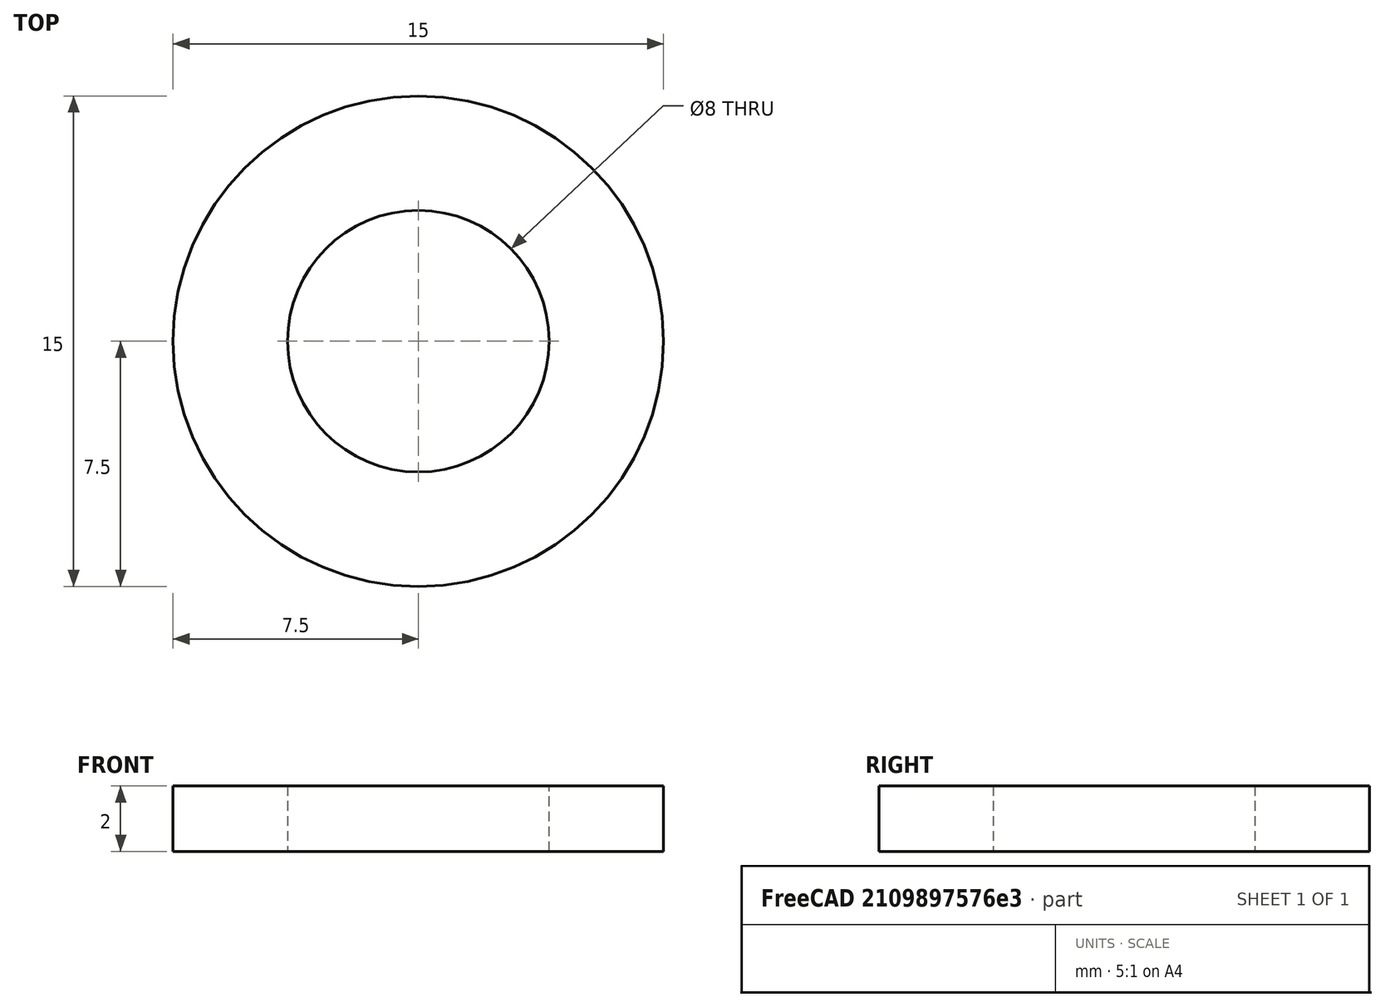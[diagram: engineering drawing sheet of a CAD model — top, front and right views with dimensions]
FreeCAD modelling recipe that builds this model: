
FCSTD DOCUMENT  (FreeCAD 0.19R24276 (Git))
Label: Ring_d8_d15_h2
License: All rights reserved
LicenseURL: http://en.wikipedia.org/wiki/All_rights_reserved
objects: Sketcher::SketchObject×1, PartDesign::Pad×1, PartDesign::Body×1
note: 4 computed .brp shape members not serialized (recipe doc carries the construction recipe); baked Part::Feature solids carry a one-line shape summary decoded from their .brp

FEATURE [Sketcher::SketchObject] Sketch
  FullyConstrained = false
  MapMode = 5
  Support = -> [XY_Plane]
  sketch-geometry (2):
    g0: Circle CenterX=0 CenterY=0 CenterZ=0 NormalX=0 NormalY=0 NormalZ=1 AngleXU=0 Radius=4
    g1: Circle CenterX=0 CenterY=0 CenterZ=0 NormalX=0 NormalY=0 NormalZ=1 AngleXU=0 Radius=7.5
  constraints (3):
    c: Coincident(g1,g0)
    c: Diameter(g1) = 15
    c: Diameter(g0) = 8
FEATURE [PartDesign::Pad] Pad
  Direction = (1,1,1)
  Length = 2
  Length2 = 100
  Profile = -> Sketch
  Type = 0
FEATURE [PartDesign::Body] Body
  Group = -> [Sketch,Pad]
  Origin = -> Origin
  Tip = -> Pad
